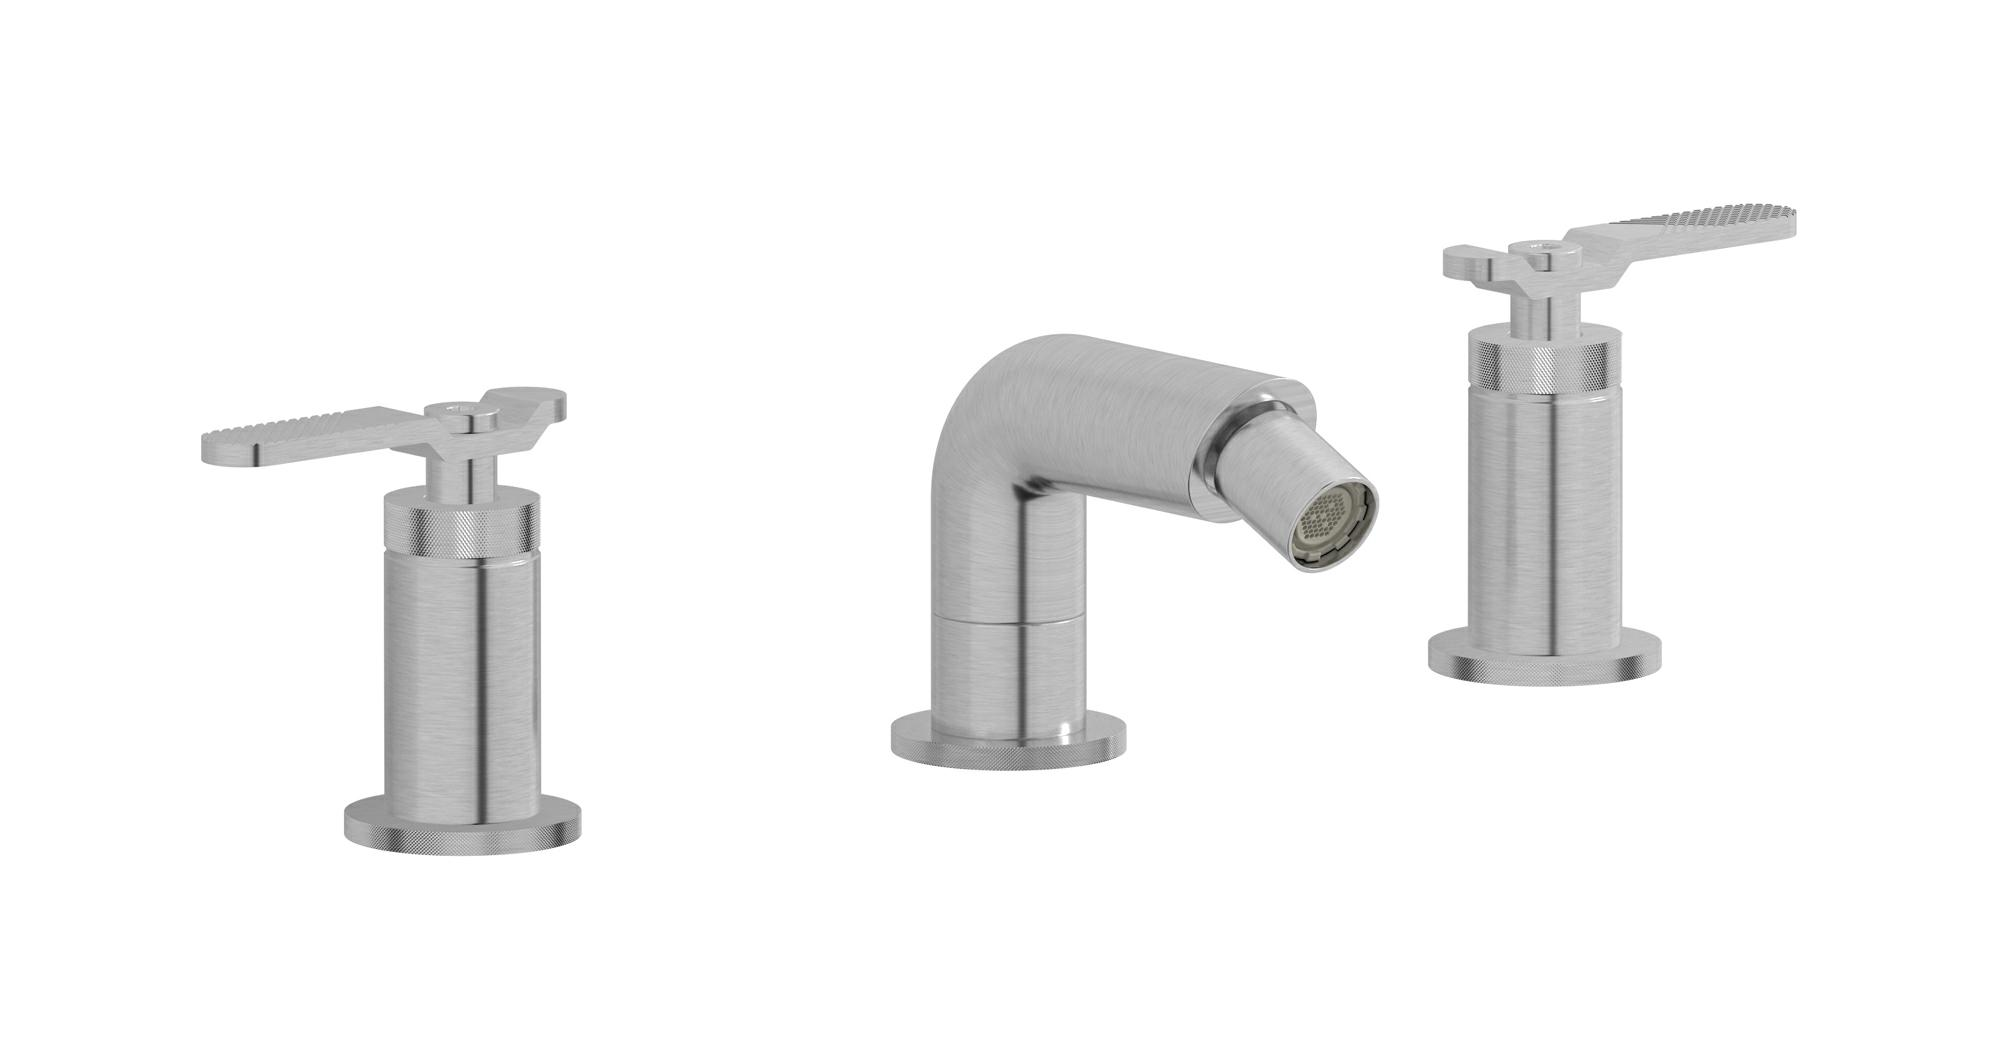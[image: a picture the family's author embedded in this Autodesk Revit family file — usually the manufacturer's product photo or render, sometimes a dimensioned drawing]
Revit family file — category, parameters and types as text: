
# Revit family: B2393
name_source: partatom
category: Apparecchi idraulici
units: mm (PartAtom-declared; Revit-internal decimal feet)

## family parameters
Basato su piano di lavoro = No
Condiviso = No
Mantieni orientamento annotazione = No
Numero OmniClass = 23.45.55.17
Punto di calcolo locali = No
Quota connettore circolare = Usa diametro
Sempre verticale = Sì
Taglio con vuoti quando caricato = No
Tipo di parte = Normale
Titolo OmniClass = Mixing Faucets

## types (13) — shared parameters
Cold water inlet = 10 mm  [stored 0.0328084 ft]
Commenti sul tipo = Three holes bidet set
Connessione CW = No
Connessione HW = No
Connessione di scarico = No
Connessione di ventilazione = No
Descrizione = Three holes bidet set
Hot water inlet = 10 mm  [stored 0.0328084 ft]
Produttore = IB Rubinetterie S.p.A.
URL = https://www.weareib.it
zero-valued in all types: Prospetto di default

## per-type parameters (varying)
| type | Finishes surface | Immagine tipo | Modello |
| Chrome | IB_Chrome | B2393CC.jpg | B2393CC |
| Black Chrome | IB_Black chrome | B2393CF.jpg | B2393CF |
| Brushed Black Chrome | IB_Brushed black chrome | B2393CS.jpg | B2393CS |
| Pale Gold | IB_Pale gold | B2393II.jpg | B2393II |
| Brushed Pale Gold | IB_brushed pale gold | B2393IS.jpg | B2393IS |
| Matt Black | IB_matt black | B2393NP.jpg | B2393NP |
| Natural Brass | IB_Brass | B2393ON.jpg | B2393ON |
| Gold | IB_gold | B2393OO.jpg | B2393OO |
| Brushed Gold | IB_brushed gold | B2393OS.jpg | B2393OS |
| Rose Gold | IB_Rose gold | B2393RS.jpg | B2393RS |
| Brushed Rose Gold | IB_Brushed rose gold | B2393SR.jpg | B2393SR |
| Brushed Nickel | IB_Brushed nickel | B2393SS.jpg | B2393SS |
| Modern Bronze | IB_Modern bronze | B2393MB.jpg | B2393MB |

note: [stored X ft] marks values corroborated as IEEE doubles in the binary element streams (Revit-internal decimal feet)
